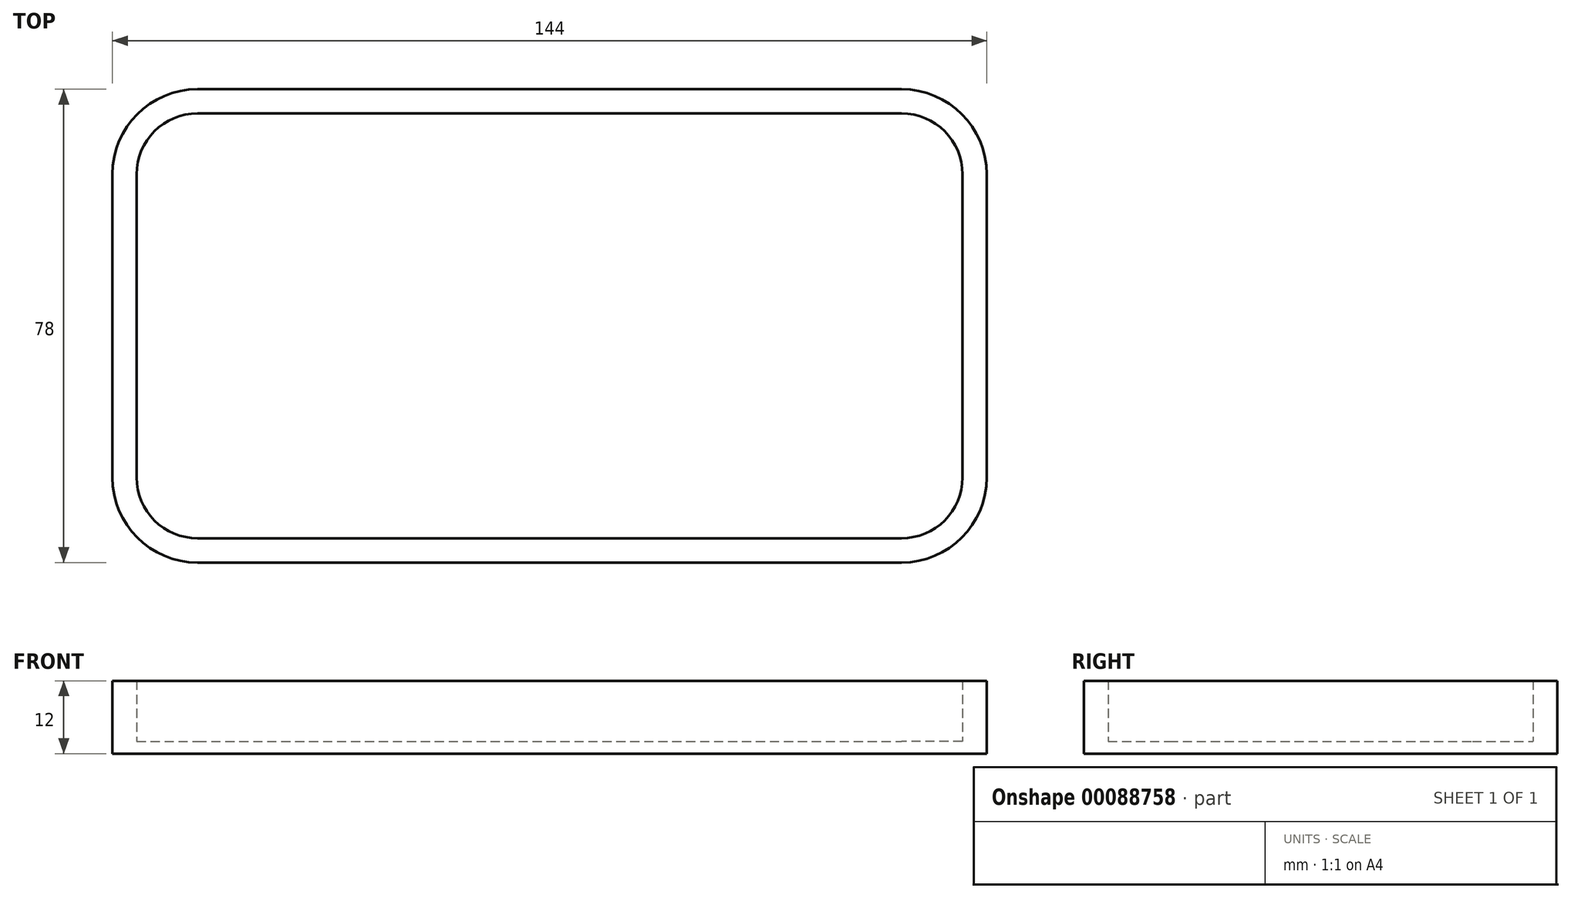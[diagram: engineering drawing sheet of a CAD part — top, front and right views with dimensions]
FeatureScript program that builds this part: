
annotation { "Feature Type Name" : "Feature", "Feature Type Description" : "" }
export const myFeature = defineFeature(function(context is Context, id is Id, definition is map)
    precondition{}
    {
        {
            var Q0;
            Q0=qCreatedBy(makeId("Top.planeOp"),FACE);
            var sketch = newSketch(context, id + "F0", { "sketchPlane" : qUnion([Q0])});
            skLineSegment(sketch, "E0.bottom", {"start": v(-58, -35) * mm, "end": v(58, -35) * mm});
            skLineSegment(sketch, "E0.top", {"start": v(-58, 35) * mm, "end": v(58, 35) * mm});
            skLineSegment(sketch, "E0.left", {"start": v(-68, -25) * mm, "end": v(-68, 25) * mm});
            skLineSegment(sketch, "E0.right", {"start": v(68, -25) * mm, "end": v(68, 25) * mm});
            skPoint(sketch, "E0.middle", {"position": v(0, 0) * mm});
            skPoint(sketch, "E1.visualSharp", {"position": v(-68, 35) * mm});
            skArc(sketch, "E1.filletArc", {"start": v(-58, 35) * mm, "mid": v(-65.07, 32.07) * mm, "end": v(-68, 25) * mm});
            skPoint(sketch, "E2.visualSharp", {"position": v(68, -35) * mm});
            skArc(sketch, "E2.filletArc", {"start": v(58, -35) * mm, "mid": v(65.07, -32.07) * mm, "end": v(68, -25) * mm});
            skPoint(sketch, "E3.visualSharp", {"position": v(68, 35) * mm});
            skArc(sketch, "E3.filletArc", {"start": v(68, 25) * mm, "mid": v(65.07, 32.07) * mm, "end": v(58, 35) * mm});
            skPoint(sketch, "E4.visualSharp", {"position": v(-68, -35) * mm});
            skArc(sketch, "E4.filletArc", {"start": v(-68, -25) * mm, "mid": v(-65.07, -32.07) * mm, "end": v(-58, -35) * mm});
            skArc(sketch, "E5.0", {"start": v(-58, 39) * mm, "mid": v(-67.9, 34.9) * mm, "end": v(-72, 25) * mm});
            skLineSegment(sketch, "E5.1", {"start": v(-72, -25) * mm, "end": v(-72, 25) * mm});
            skLineSegment(sketch, "E5.2", {"start": v(-58, 39) * mm, "end": v(58, 39) * mm});
            skArc(sketch, "E5.3", {"start": v(-72, -25) * mm, "mid": v(-67.9, -34.9) * mm, "end": v(-58, -39) * mm});
            skArc(sketch, "E5.4", {"start": v(72, 25) * mm, "mid": v(67.9, 34.9) * mm, "end": v(58, 39) * mm});
            skLineSegment(sketch, "E5.5", {"start": v(72, -25) * mm, "end": v(72, 25) * mm});
            skArc(sketch, "E5.6", {"start": v(58, -39) * mm, "mid": v(67.9, -34.9) * mm, "end": v(72, -25) * mm});
            skLineSegment(sketch, "E5.7", {"start": v(-58, -39) * mm, "end": v(58, -39) * mm});
            skSolve(sketch);
        }
        {
            var Q0;
            Q0=makeQuery(id+"F0.imprint","IMPRINT",FACE,{"disambiguationData":[TD([[makeQuery(id+"F0.imprint","IMPRINT",EDGE,{"derivedFrom":sQuery(id+"F0.wireOp",EDGE,"E0.bottom")}),1.0]])]});
            extrude(context, id + "F1", {"entities" : qUnion([Q0]), "depth" : 2 * mm});
        }
        {
            var Q0;
            Q0=makeQuery(id+"F0.imprint","IMPRINT",FACE,{"disambiguationData":[TD([[makeQuery(id+"F0.imprint","IMPRINT",EDGE,{"derivedFrom":sQuery(id+"F0.wireOp",EDGE,"E0.bottom")}),-1.0]])]});
            extrude(context, id + "F2", {"entities" : qUnion([Q0]), "operationType" : NewBodyOperationType.ADD, "depth" : 12 * mm});
        }
    });
